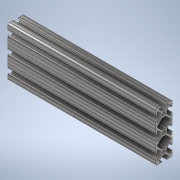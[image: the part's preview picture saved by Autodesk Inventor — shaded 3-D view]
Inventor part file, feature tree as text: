
AUTODESK INVENTOR PART (.ipt)
format: ipt  version: 2020 (Build 240168000, 168)  size: 379,392 bytes
history: native  units: in
note: dims shown in document units (in); Inventor stores cm internally (conversion verified against a paired STEP export)
features: sketch x2, extrude x1
ambient origin geometry x8: Origin, YZ Plane, XZ Plane, XY Plane, X Axis, Y Axis, Z Axis, Center Point
bodies: Solid1 (feature_tree)
feature tree (3):
  extrude  "Extrusion1"  [1 undecoded]
  sketch  "Sketch2"
  sketch  "Sketch1"  dims[d0=9.0in d1=0.0in]
note: 1 required parameter value undecoded (feature->parameter linkage not recoverable at this tier; creation-order binding heuristic only, values carry confidence <= 0.55)
